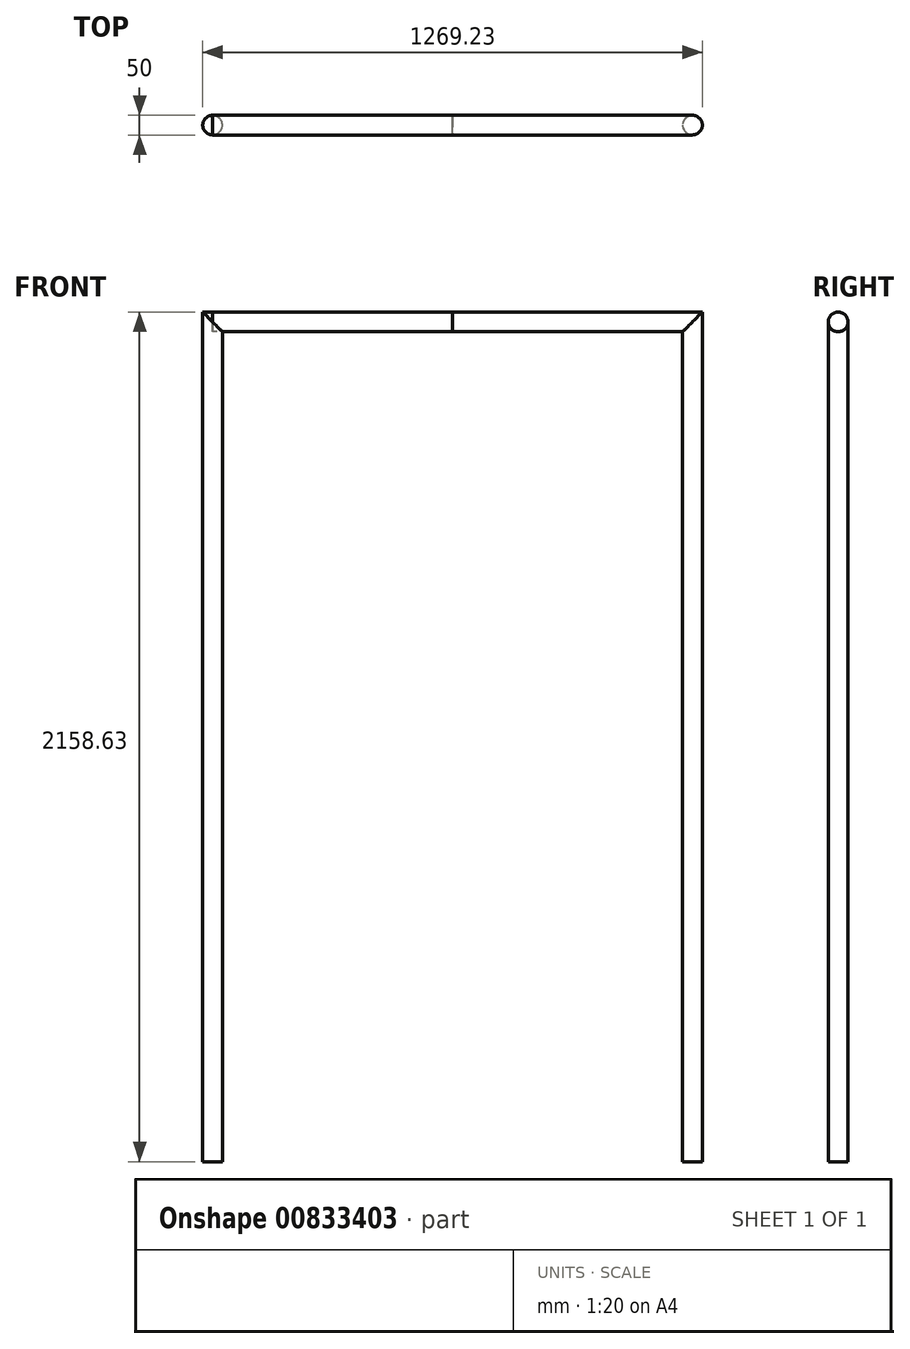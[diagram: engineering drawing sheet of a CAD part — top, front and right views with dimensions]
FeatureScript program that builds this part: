
annotation { "Feature Type Name" : "Feature", "Feature Type Description" : "" }
export const myFeature = defineFeature(function(context is Context, id is Id, definition is map)
    precondition{}
    {
        {
            var Q0;
            Q0=qCreatedBy(makeId("Top.planeOp"),FACE);
            var sketch = newSketch(context, id + "F0", { "sketchPlane" : qUnion([Q0])});
            skCircle(sketch, "E0", {"center": v(0, 0) * mm, "radius": 25 * mm});
            skSolve(sketch);
        }
        {
            var Q0;
            Q0=qCreatedBy(makeId("Front.planeOp"),FACE);
            var sketch = newSketch(context, id + "F1", { "sketchPlane" : qUnion([Q0])});
            skLineSegment(sketch, "E1", {"start": v(0, 0) * mm, "end": v(0, 2133.6) * mm});
            skLineSegment(sketch, "E2", {"start": v(0, 2133.6) * mm, "end": v(1219.2, 2133.6) * mm});
            skLineSegment(sketch, "E3", {"start": v(1219.2, 2133.6) * mm, "end": v(1219.2, 0) * mm});
            skLineSegment(sketch, "E4", {"start": v(0, 2133.6) * mm, "end": v(609.6, 2133.6) * mm});
            skSolve(sketch);
        }
        {
            var Q0;
            Q0=makeQuery(id+"F0.imprint","IMPRINT",FACE,{"disambiguationData":[TD([[makeQuery(id+"F0.imprint","IMPRINT",EDGE,{"derivedFrom":sQuery(id+"F0.wireOp",EDGE,"E0")}),1.0]])]});
            var Q1;
            Q1=sQuery(id+"F1.wireOp",EDGE,"E1");
            var Q2;
            Q2=sQuery(id+"F1.wireOp",EDGE,"E4");
            sweep(context, id + "F2", {"profiles" : qUnion([Q0]), "path" : qUnion([Q1, Q2])});
        }
        {
            var Q0;
            Q0=sQuery(id+"F1.wireOp",VERTEX,"E3.end");
            var Q1;
            Q1=sQuery(id+"F1.wireOp",EDGE,"E3");
            cPlane(context, id + "F3", {"entities" : qUnion([Q0, Q1]), "cplaneType" : CPlaneType.LINE_POINT, "offset" : 25.4 * mm, "width" : 152.4 * mm, "height" : 152.4 * mm});
        }
        {
            var Q0;
            Q0=qCreatedBy(id+"F3.planeOp",FACE);
            var sketch = newSketch(context, id + "F4", { "sketchPlane" : qUnion([Q0])});
            skPoint(sketch, "E5", {"position": v(1219.23, 0) * mm});
            skCircle(sketch, "E6", {"center": v(1219.23, 0) * mm, "radius": 25 * mm});
            skSolve(sketch);
        }
        {
            var Q0;
            Q0=makeQuery(id+"F4.imprint","IMPRINT",FACE,{"disambiguationData":[TD([[makeQuery(id+"F4.imprint","IMPRINT",EDGE,{"derivedFrom":sQuery(id+"F4.wireOp",EDGE,"E6")}),1.0]])]});
            var Q1;
            Q1=sQuery(id+"F1.wireOp",EDGE,"E3");
            var Q2;
            Q2=sQuery(id+"F1.wireOp",EDGE,"E2");
            sweep(context, id + "F5", {"profiles" : qUnion([Q0]), "path" : qUnion([Q1, Q2])});
        }
    });
